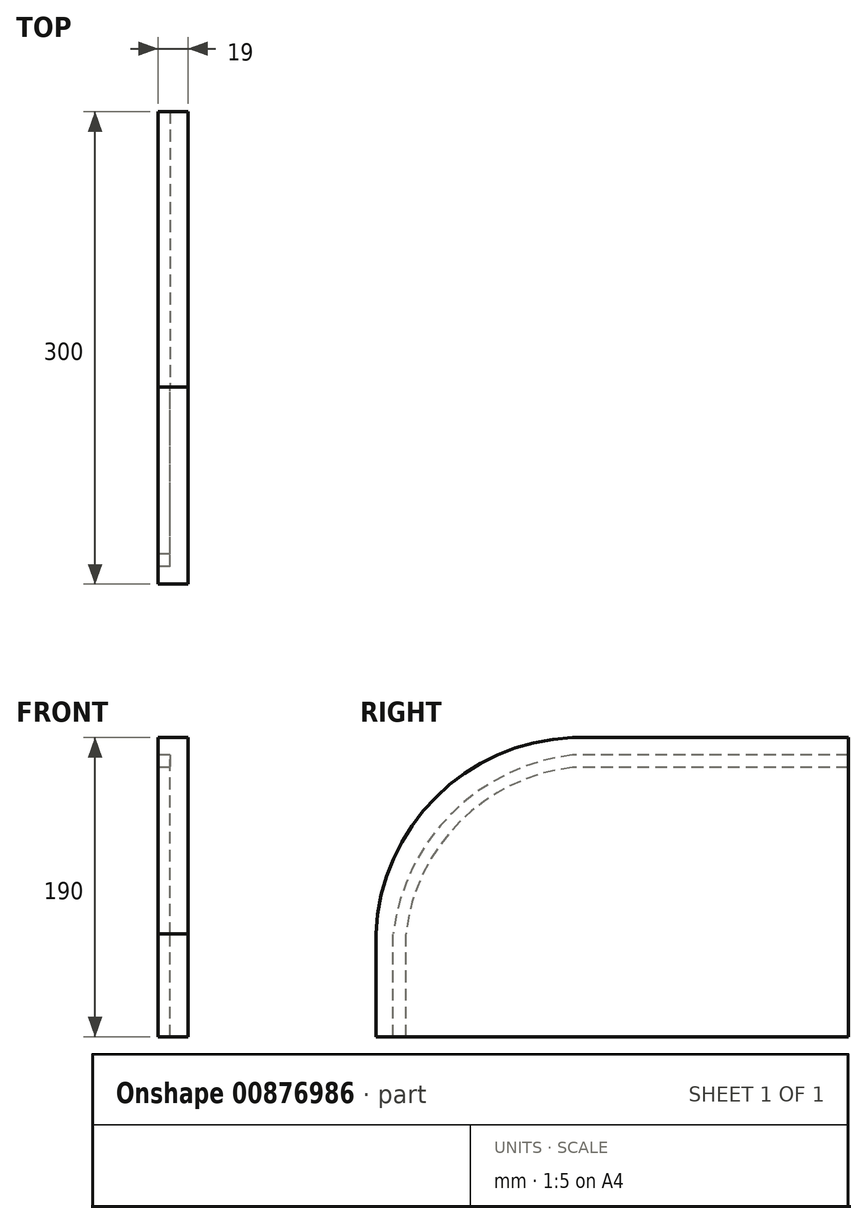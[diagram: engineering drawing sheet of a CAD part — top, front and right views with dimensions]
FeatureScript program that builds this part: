
annotation { "Feature Type Name" : "Feature", "Feature Type Description" : "" }
export const myFeature = defineFeature(function(context is Context, id is Id, definition is map)
    precondition{}
    {
        {
            var Q0;
            Q0=qCreatedBy(makeId("Right.planeOp"),FACE);
            var sketch = newSketch(context, id + "F0", { "sketchPlane" : qUnion([Q0]), "disableImprinting" : false});
            skLineSegment(sketch, "E0.bottom", {"start": v(-25, 95) * mm, "end": v(150, 95) * mm});
            skLineSegment(sketch, "E0.top", {"start": v(-150, -95) * mm, "end": v(150, -95) * mm});
            skLineSegment(sketch, "E0.left", {"start": v(-150, -29.82) * mm, "end": v(-150, -95) * mm});
            skLineSegment(sketch, "E0.right", {"start": v(150, 95) * mm, "end": v(150, -95) * mm});
            skPoint(sketch, "E0.middle", {"position": v(0, 0) * mm});
            skPoint(sketch, "E1", {"position": v(-150, -40) * mm});
            skPoint(sketch, "E2", {"position": v(-25, 95) * mm});
            skArc(sketch, "E3", {"start": v(-25, 95) * mm, "mid": v(-115.49, 53.42) * mm, "end": v(-150, -40) * mm});
            skPoint(sketch, "E4.orphan", {"position": v(-150, 95) * mm});
            skSolve(sketch);
        }
        {
            var Q0;
            {var subQ5=sQuery(id+"F0.wireOp",EDGE,"E0.bottom");Q0=makeQuery(id+"F0.imprint","IMPRINT",FACE,{"disambiguationData":[TD([[makeQuery(id+"F0.imprint","IMPRINT",EDGE,{"derivedFrom":subQ5}),-1.0]])]});}
            extrude(context, id + "F1", {"entities" : qUnion([Q0]), "depth" : 19 * mm, "offsetDistance" : 25 * mm});
        }
        {
            var Q0;
            Q0=makeQuery(id+"F1.opExtrude","CAP_FACE",FACE,{"disambiguationData":[OSD([sQuery(id+"F0.wireOp",EDGE,"E0.bottom"),sQuery(id+"F0.wireOp",EDGE,"E0.top"),sQuery(id+"F0.wireOp",EDGE,"E0.left"),sQuery(id+"F0.wireOp",EDGE,"E0.right"),sQuery(id+"F0.wireOp",EDGE,"E3")])],"isStart":true});
            var sketch = newSketch(context, id + "F2", { "sketchPlane" : qUnion([Q0]), "disableImprinting" : false});
            skPoint(sketch, "E5", {"position": v(-150, 84) * mm});
            skLineSegment(sketch, "E6", {"start": v(-150, 84) * mm, "end": v(25, 84) * mm});
            skPoint(sketch, "E7", {"position": v(-150, 76) * mm});
            skLineSegment(sketch, "E8", {"start": v(-150, 76) * mm, "end": v(25, 76) * mm});
            skPoint(sketch, "E9", {"position": v(139, -95) * mm});
            skPoint(sketch, "E10", {"position": v(131, -95) * mm});
            skLineSegment(sketch, "E11", {"start": v(139, -95) * mm, "end": v(139, -29.82) * mm});
            skLineSegment(sketch, "E12", {"start": v(131, -95) * mm, "end": v(131, -29.82) * mm});
            skArc(sketch, "E13", {"start": v(139, -29.82) * mm, "mid": v(101.75, 46.88) * mm, "end": v(25, 84) * mm});
            skArc(sketch, "E14", {"start": v(131, -29.82) * mm, "mid": v(96.54, 41.66) * mm, "end": v(25, 76) * mm});
            skSolve(sketch);
        }
        {
            var Q0;
            {var subQ1=sQuery(id+"F2.wireOp",EDGE,"E6");Q0=makeQuery(id+"F2.imprint","IMPRINT",FACE,{"disambiguationData":[TD([[makeQuery(id+"F2.imprint","IMPRINT",EDGE,{"derivedFrom":subQ1}),-1.0]])]});}
            extrude(context, id + "F3", {"entities" : qUnion([Q0]), "operationType" : NewBodyOperationType.REMOVE, "flatOperationType" : FlatOperationType.REMOVE, "oppositeDirection" : true, "depth" : 7.5 * mm, "offsetDistance" : 25 * mm, "domain" : OperationDomain.MODEL});
        }
    });
